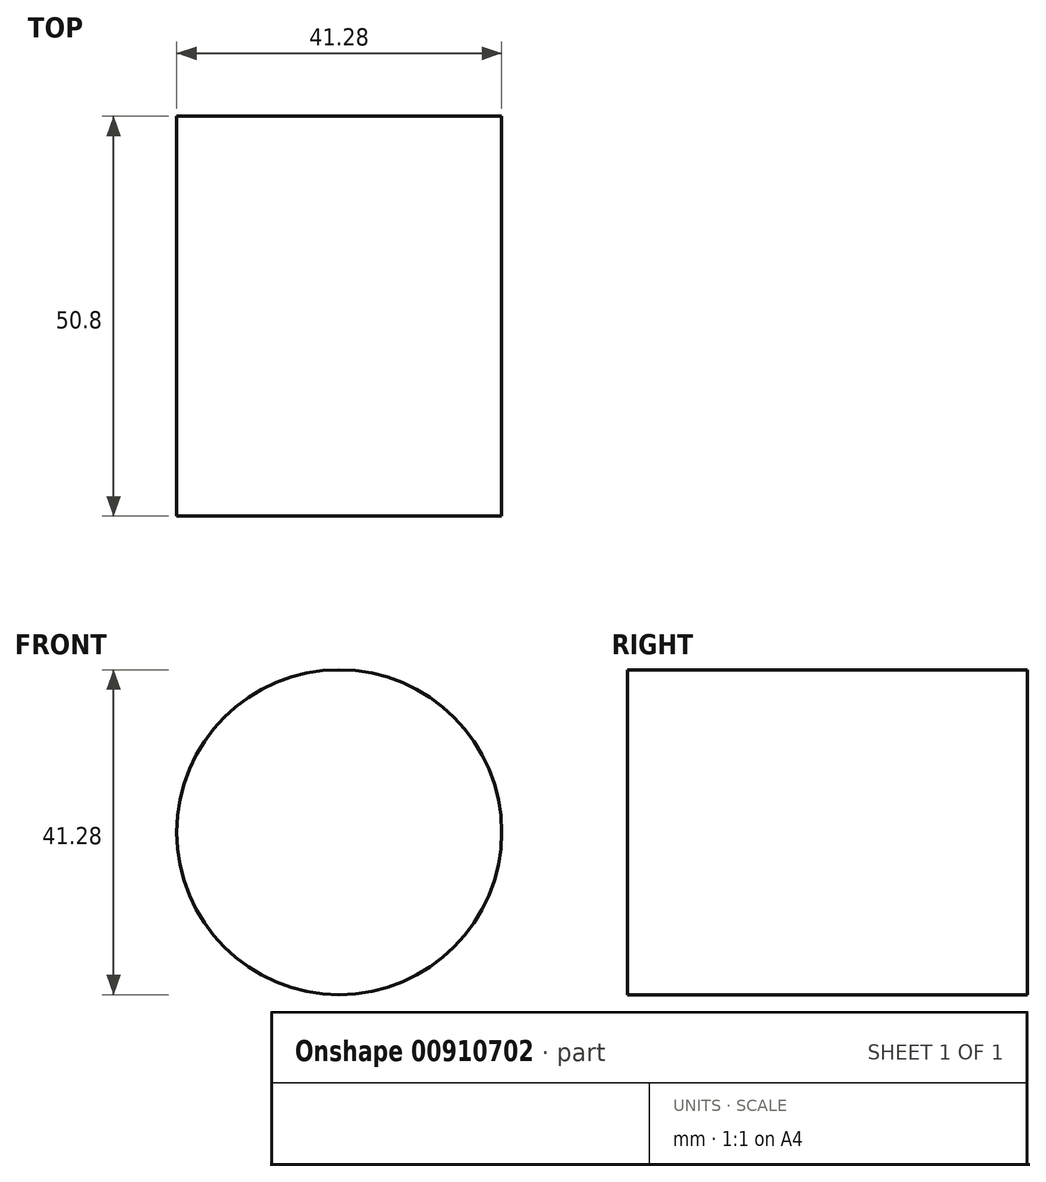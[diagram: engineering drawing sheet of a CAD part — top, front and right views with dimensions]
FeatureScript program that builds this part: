
annotation { "Feature Type Name" : "Feature", "Feature Type Description" : "" }
export const myFeature = defineFeature(function(context is Context, id is Id, definition is map)
    precondition{}
    {
        {
            var Q0;
            Q0=qCreatedBy(makeId("Front.planeOp"),FACE);
            var sketch = newSketch(context, id + "F0", { "sketchPlane" : qUnion([Q0])});
            skCircle(sketch, "E0", {"center": v(0, 0) * mm, "radius": 20.64 * mm});
            skSolve(sketch);
        }
        {
            var Q0;
            Q0=makeQuery(id+"F0.imprint","IMPRINT",FACE,{"disambiguationData":[TD([[makeQuery(id+"F0.imprint","IMPRINT",EDGE,{"derivedFrom":sQuery(id+"F0.wireOp",EDGE,"E0")}),1.0]])]});
            extrude(context, id + "F1", {"entities" : qUnion([Q0]), "depth" : 50.8 * mm, "offsetDistance" : 25.4 * mm});
        }
    });
